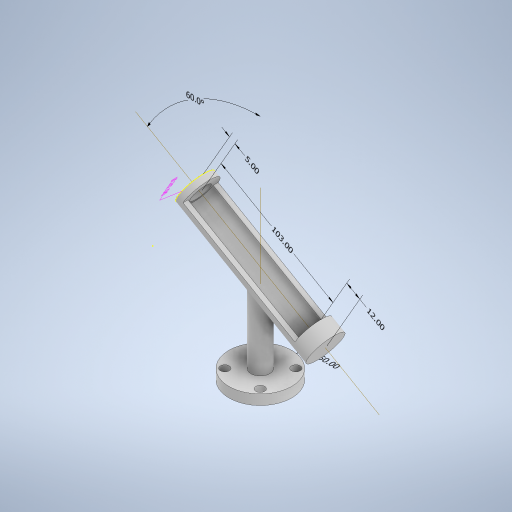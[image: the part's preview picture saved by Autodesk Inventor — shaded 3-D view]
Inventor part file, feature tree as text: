
AUTODESK INVENTOR PART (.ipt)
format: ipt  version: 2024.3 (Build 283343000, 343)  size: 363,520 bytes
history: native  units: mm
features: sketch x11, other x10, extrude x9, plane x4
ambient origin geometry x8: Origin, YZ Plane, XZ Plane, XY Plane, X Axis, Y Axis, Z Axis, Center Point
bodies: Body1 (feature_tree)
feature tree (34):
  other  "Sólido1"
  other  "Anotaciones"
  extrude  "Extrusión1"  Depth=8.0mm TaperAngle=0.0deg
  extrude  "Extrusión2"  Depth=7.0mm
  extrude  "Extrusión3"  Depth=7.0mm
  sketch  "Boceto4"  dims[d10=7.0mm d11=8.0mm d12=0.0mm]
  plane  "Plano de trabajo7"
  plane  "Plano de trabajo6"
  extrude  "Extrusión4"  Depth=8.0mm TaperAngle=0.0deg
  extrude  "Extrusión5"  Depth=70.0mm TaperAngle=0.0deg
  extrude  "Extrusión6"  TaperAngle=120.0deg  [1 undecoded]
  extrude  "Extrusión7"  Depth=28.0mm
  plane  "Plano de trabajo8"
  extrude  "Extrusión8"  Depth=5.0mm TaperAngle=0.0deg
  sketch  "Boceto16"  dims[d31=5.0mm d32=0.0mm]
  plane  "Plano de trabajo9"
  extrude  "Extrusión9"  Depth=115.0mm
  other  "Eje de trabajo1"
  other  "Eje de trabajo2"
  sketch  "Boceto1"  dims[d0=50.0mm d1=8.0mm d2=0.0mm]
  sketch  "Boceto2"  dims[d3=40.0mm d7=7.0mm]
  sketch  "Boceto3"  dims[d8=7.0mm d9=7.0mm]
  sketch  "Boceto10"  dims[d13=15.0mm d14=70.0mm d15=0.0mm]
  sketch  "Boceto12"  dims[d19=30.0deg d20=120.0deg]
  sketch  "Boceto13"  dims[d21=20.0mm d22=28.0mm]
  sketch  "Boceto14"  dims[d23=120.0mm d24=0.0mm d26=5.0mm d27=0.0mm]
  sketch  "Boceto15"  dims[d28=115.0mm d29=0.0mm d30=15.6mm]
  sketch  "Boceto17"  dims[d45=20.0mm d46=-5.0mm d47=20.0mm d48=15.0mm d49=7.0mm d50=0.0mm d51=5.0mm d52=103.0mm d53=90.0deg d54=28.0mm d55=0.0mm d41=18.92594mm d42=20.0mm d43=45.496035mm d44=50.0mm d56=103.0mm d57=-118.217001mm d58=-147.896388mm d59=60.0deg d60=5.0mm d61=12.0mm]
  other  "Cota de diámetro 1"
  other  "Cota de diámetro 2"
  other  "Cota lineal 2"
  other  "Cota angular 1"
  other  "Cota lineal 3"
  other  "Cota lineal 4"
note: 1 required parameter value undecoded (feature->parameter linkage not recoverable at this tier; creation-order binding heuristic only, values carry confidence <= 0.55)
